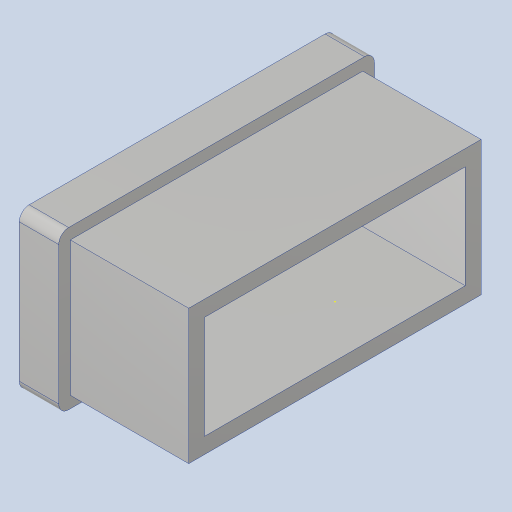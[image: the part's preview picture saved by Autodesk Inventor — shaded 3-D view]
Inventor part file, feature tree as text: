
AUTODESK INVENTOR PART (.ipt)
format: ipt  version: 2023.4 (Build 274418000, 418)  size: 297,984 bytes
history: native  units: in
note: dims shown in document units (in); Inventor stores cm internally (conversion verified against a paired STEP export)
features: sketch x4, extrude x2, shell x1, fillet x1, emboss x1
ambient origin geometry x8: Origin, YZ Plane, XZ Plane, XY Plane, X Axis, Y Axis, Z Axis, Center Point
bodies: Solid1 (feature_tree)
feature tree (9):
  extrude  "Extrusion1"  Depth=1.0in
  extrude  "Extrusion2"  Depth=0.0078in
  shell  "Shell1"  Thickness=0.25in
  fillet  "Fillet1"  Radius=0.0625in
  emboss  "Emboss1"
  sketch  "Sketch4"  dims[d10=0.011in d11=0.75in d12=0.0in d13=0.1in d14=0.0625in d15=0.25in d16=0.0in]
  sketch  "Sketch1"  dims[d0=2.0in d1=1.0in]
  sketch  "Sketch2"  dims[d4=0.0625in d5=0.0078in d6=0.25in d7=0.0in d8=0.0625in]
  sketch  "Sketch3"  dims[d9=0.0625in]
